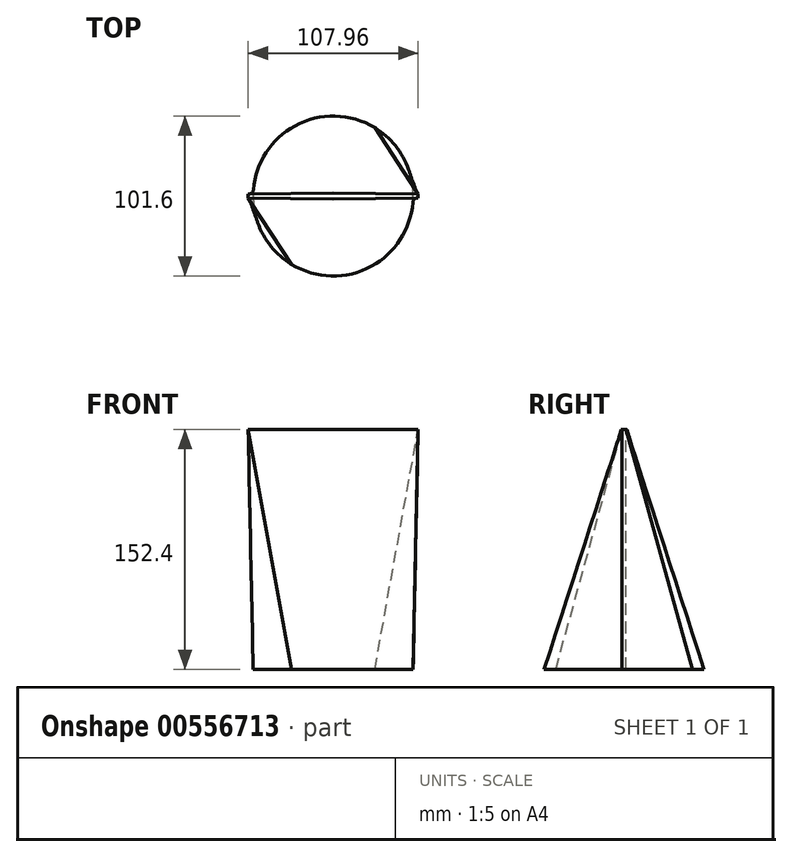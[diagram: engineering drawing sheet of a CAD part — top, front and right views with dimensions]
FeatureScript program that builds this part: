
annotation { "Feature Type Name" : "Feature", "Feature Type Description" : "" }
export const myFeature = defineFeature(function(context is Context, id is Id, definition is map)
    precondition{}
    {
        {
            var Q0;
            Q0=qCreatedBy(makeId("Top.planeOp"),FACE);
            cPlane(context, id + "F0", {"entities" : qUnion([Q0]), "cplaneType" : CPlaneType.OFFSET, "offset" : 152.4 * mm, "width" : 152.4 * mm, "height" : 152.4 * mm});
        }
        {
            var Q0;
            Q0=qCreatedBy(makeId("Top.planeOp"),FACE);
            var sketch = newSketch(context, id + "F1", { "sketchPlane" : qUnion([Q0])});
            skCircle(sketch, "E0", {"center": v(0, 0) * mm, "radius": 50.8 * mm});
            skSolve(sketch);
        }
        {
            var Q0;
            Q0=qCreatedBy(id+"F0.planeOp",FACE);
            var sketch = newSketch(context, id + "F2", { "sketchPlane" : qUnion([Q0])});
            skLineSegment(sketch, "E1.left", {"start": v(53.98, -1.27) * mm, "end": v(53.98, 1.27) * mm});
            skLineSegment(sketch, "E1.right", {"start": v(-53.98, -1.27) * mm, "end": v(-53.98, 1.27) * mm});
            skPoint(sketch, "E1.middle", {"position": v(0, 0) * mm});
            skLineSegment(sketch, "E2", {"start": v(-53.98, 1.27) * mm, "end": v(0, 1.9) * mm});
            skLineSegment(sketch, "E3", {"start": v(0, 1.9) * mm, "end": v(53.98, 1.27) * mm});
            skLineSegment(sketch, "E4", {"start": v(53.98, -1.27) * mm, "end": v(0, -1.9) * mm});
            skLineSegment(sketch, "E5", {"start": v(0, -1.9) * mm, "end": v(-53.98, -1.27) * mm});
            skSolve(sketch);
        }
        {
            var Q0;
            Q0=makeQuery(id+"F1.imprint","IMPRINT",FACE,{"disambiguationData":[TD([[makeQuery(id+"F1.imprint","IMPRINT",EDGE,{"derivedFrom":sQuery(id+"F1.wireOp",EDGE,"E0")}),1.0]])]});
            var Q1;
            Q1=makeQuery(id+"F2.imprint","IMPRINT",FACE,{"disambiguationData":[TD([[makeQuery(id+"F2.imprint","IMPRINT",EDGE,{"derivedFrom":sQuery(id+"F2.wireOp",EDGE,"E1.left")}),1.0]])]});
            loft(context, id + "F3", {"sheetProfilesArray" : [{ "sheetProfileEntities" : qUnion([Q0]) }, { "sheetProfileEntities" : qUnion([Q1]) }]});
        }
    });
